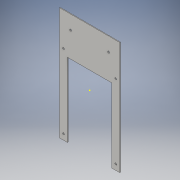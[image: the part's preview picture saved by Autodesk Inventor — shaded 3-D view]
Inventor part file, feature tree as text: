
AUTODESK INVENTOR PART (.ipt)
format: ipt  version: 2016 (Build 200138000, 138)  size: 152,576 bytes
history: native  units: in
note: dims shown in document units (in); Inventor stores cm internally (conversion verified against a paired STEP export)
features: sketch x5, extrude x3, hole x2, other x1
ambient origin geometry x8: Origin, YZ Plane, XZ Plane, XY Plane, X Axis, Y Axis, Z Axis, Center Point
bodies: Solid1 (feature_tree)
feature tree (11):
  extrude  "Extrusion1"  Depth=10.135in
  hole  "Hole1"  [1 undecoded]
  extrude  "Extrusion2"  Depth=3.0in
  hole  "Hole2"  [1 undecoded]
  other  "battery_buzzer"
  extrude  "Extrusion3"  Depth=0.7in
  sketch  "Sketch1"  dims[d0=5.4in d1=10.135in]
  sketch  "Sketch2"  dims[d2=0.0625in d3=0.0in d4=0.35in]
  sketch  "Sketch4"  dims[d5=3.0in d6=3.0in]
  sketch  "Sketch5"  dims[d7=0.35in d8=0.165in]
  sketch  "Sketch10"  dims[d9=0.5in d10=0.35in d11=0.35in d12=0.5in d13=0.165in d14=0.165in d15=0.75in d16=0.375in d17=0.25in d18=0.5635in d19=1.0in d20=0.8108in d21=0.165in d22=0.165in d23=0.27in d24=0.27in d25=1.315in d26=2.0in d27=1.315in d28=1.135in d29=1.135in d30=1.135in d31=1.135in d32=2.0in d33=2.0in d34=2.0in d35=0.125in d36=0.0in d37=1.25in d38=3.412in d39=1.25in d40=0.994in d41=0.176in d42=0.75in d43=0.375in d44=0.25in d45=0.5635in d46=1.0in d47=0.8108in d48=3.5in d49=0.7in d50=0.7in d51=0.125in d52=0.0in]
note: 2 required parameter values undecoded (feature->parameter linkage not recoverable at this tier; creation-order binding heuristic only, values carry confidence <= 0.55)
